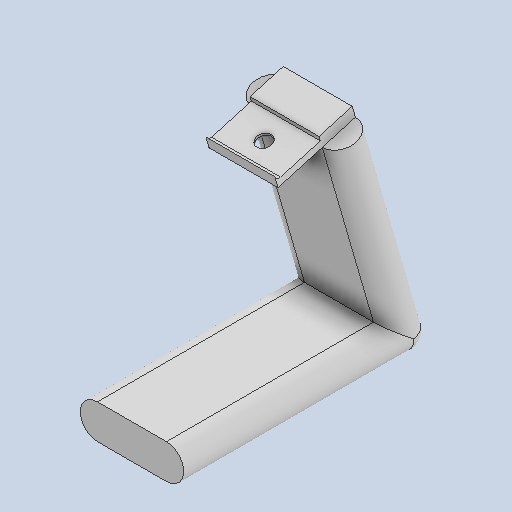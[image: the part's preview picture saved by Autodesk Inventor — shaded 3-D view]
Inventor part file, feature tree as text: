
AUTODESK INVENTOR PART (.ipt)
format: ipt  version: 2023 (Build 270158000, 158)  size: 335,872 bytes
history: native  units: in
note: dims shown in document units (in); Inventor stores cm internally (conversion verified against a paired STEP export)
features: sketch x6, extrude x4, fillet x3, sweep x1
ambient origin geometry x8: Origin, YZ Plane, XZ Plane, XY Plane, X Axis, Y Axis, Z Axis, Center Point
bodies: Solid1 (feature_tree)
feature tree (14):
  sweep  "Sweep1"
  fillet  "Fillet1"  Radius=0.5906in
  extrude  "Extrusion1"  TaperAngle=0.0deg  [1 undecoded]
  extrude  "Extrusion2"  Depth=0.1969in
  fillet  "Fillet3"  Radius=0.1969in
  extrude  "Extrusion3"  Depth=0.0787in
  extrude  "Extrusion4"  Depth=0.0787in
  fillet  "Fillet4"  Radius=0.0787in
  sketch  "Sketch1"  dims[d0=3.937in d1=90.0deg d2=0.5906in]
  sketch  "Sketch2"  dims[d3=0.5906in d4=0.0in d5=0.0in]
  sketch  "Sketch3"  dims[d6=0.2662in d8=1.378in d9=0.1969in d10=0.0in]
  sketch  "Sketch4"  dims[d11=0.1969in d12=0.0in d13=0.0787in]
  sketch  "Sketch5"  dims[d14=0.0787in d15=0.0in d16=0.0787in d17=0.0787in d18=0.0in]
  sketch  "Sketch6"  dims[d19=0.0787in]
note: 1 required parameter value undecoded (feature->parameter linkage not recoverable at this tier; creation-order binding heuristic only, values carry confidence <= 0.55)
